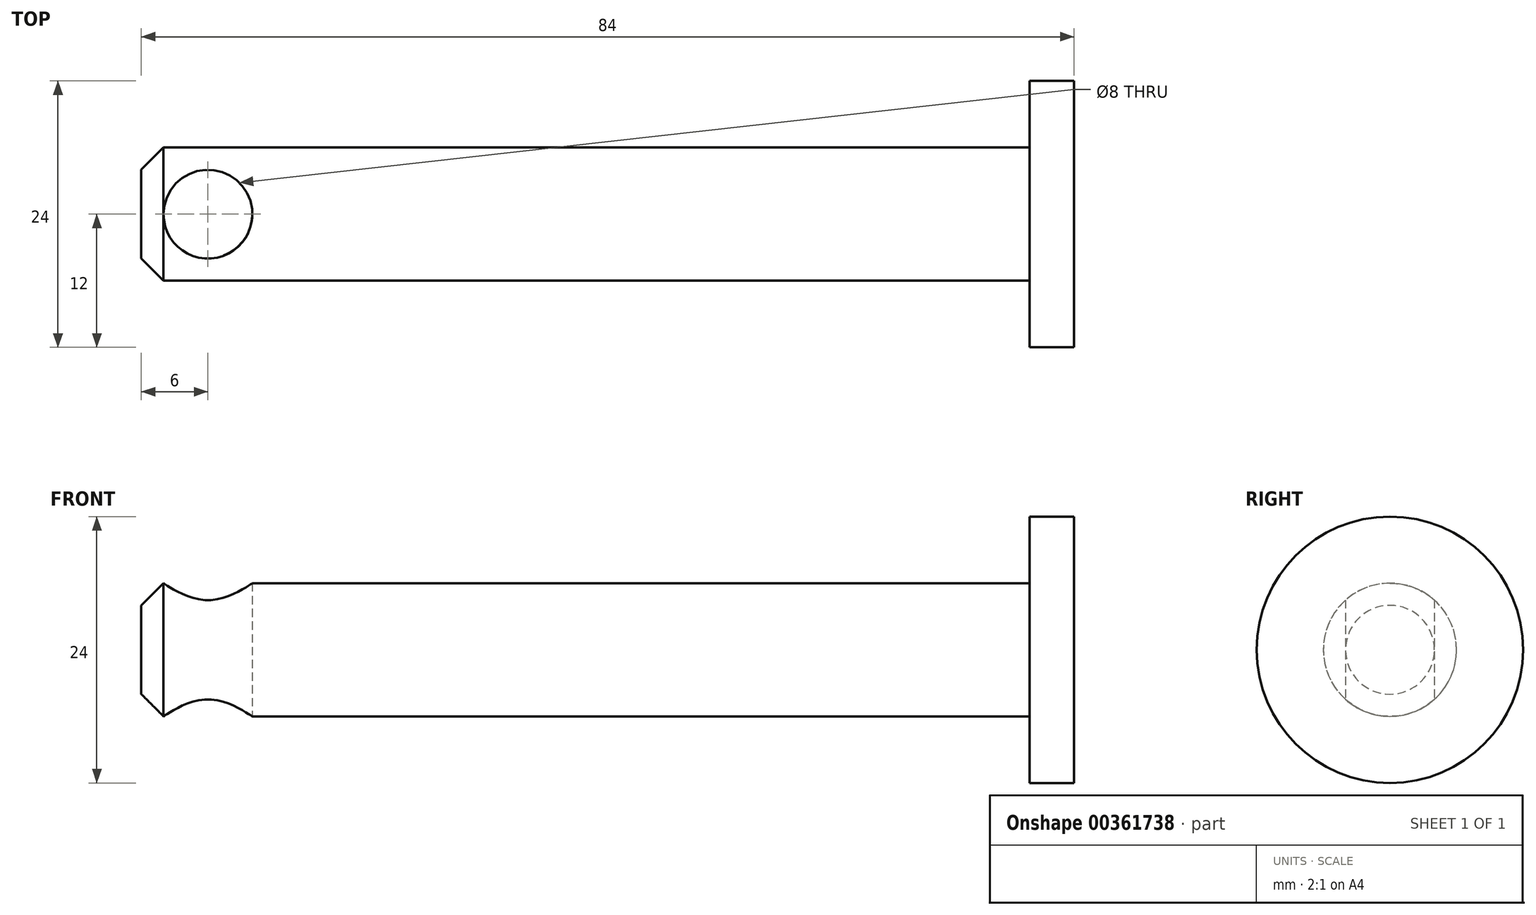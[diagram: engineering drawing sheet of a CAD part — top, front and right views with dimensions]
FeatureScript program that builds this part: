
annotation { "Feature Type Name" : "Feature", "Feature Type Description" : "" }
export const myFeature = defineFeature(function(context is Context, id is Id, definition is map)
    precondition{}
    {
        {
            var Q0;
            Q0=qCreatedBy(makeId("Top.planeOp"),FACE);
            var sketch = newSketch(context, id + "F0", { "sketchPlane" : qUnion([Q0])});
            skLineSegment(sketch, "E0", {"start": v(0, 0) * mm, "end": v(84, 0) * mm});
            skLineSegment(sketch, "E1", {"start": v(84, 0) * mm, "end": v(84, 12) * mm});
            skLineSegment(sketch, "E2", {"start": v(84, 12) * mm, "end": v(80, 12) * mm});
            skLineSegment(sketch, "E3", {"start": v(80, 12) * mm, "end": v(80, 6) * mm});
            skLineSegment(sketch, "E4", {"start": v(80, 6) * mm, "end": v(0, 6) * mm});
            skLineSegment(sketch, "E5", {"start": v(0, 6) * mm, "end": v(0, 0) * mm});
            skSolve(sketch);
        }
        {
            var Q0;
            Q0 = qSketchRegion(id + "F0", true);
            var Q1;
            Q1=sQuery(id+"F0.wireOp",EDGE,"E0");
            revolve(context, id + "F1", {"entities" : qUnion([Q0]), "axis" : qUnion([Q1]), "revolveType" : RevolveType.FULL});
        }
        {
            var Q0;
            Q0=qCreatedBy(makeId("Top.planeOp"),FACE);
            var sketch = newSketch(context, id + "F2", { "sketchPlane" : qUnion([Q0])});
            skCircle(sketch, "E6", {"center": v(6, 0) * mm, "radius": 4 * mm});
            skSolve(sketch);
        }
        {
            var Q0;
            Q0 = qSketchRegion(id + "F2", true);
            extrude(context, id + "F3", {"entities" : qUnion([Q0]), "operationType" : NewBodyOperationType.REMOVE, "endBound" : BoundingType.SYMMETRIC, "depth" : 25 * mm});
        }
        {
            var Q0;
            Q0=makeQuery(id+"F1.opRevolve","SWEPT_EDGE",EDGE,{"disambiguationData":[OSD([sQuery(id+"F0.wireOp",EDGE,"E4"),sQuery(id+"F0.wireOp",EDGE,"E5")])]});
            chamfer(context, id + "F4", {"entities" : qUnion([Q0]), "width" : 2 * mm, "tangentPropagation" : true});
        }
    });
